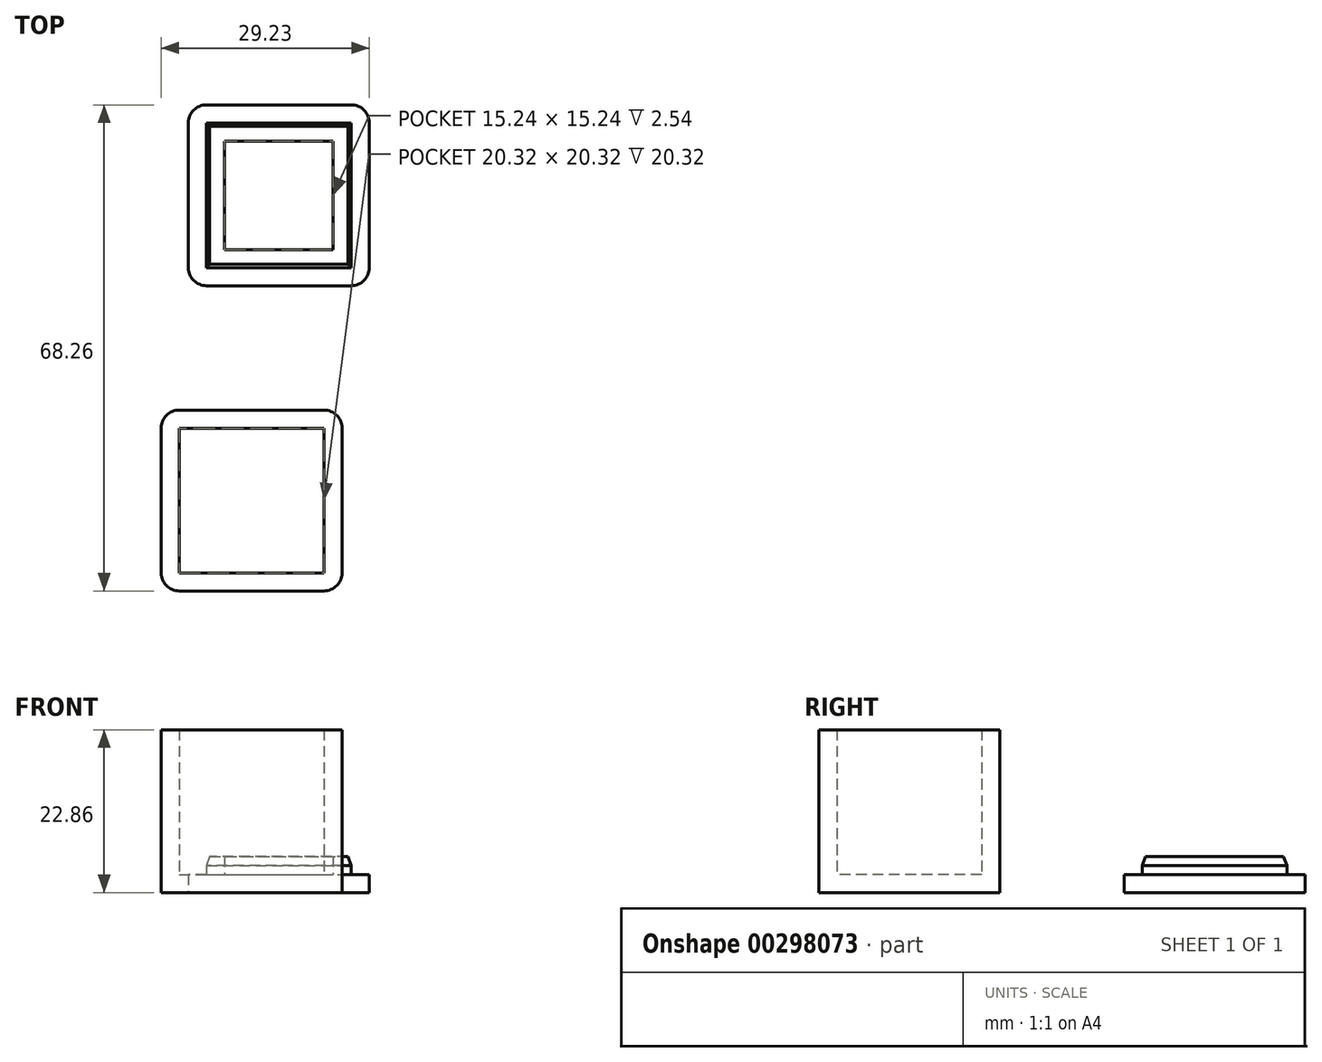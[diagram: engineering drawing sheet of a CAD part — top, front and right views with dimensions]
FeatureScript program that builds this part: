
annotation { "Feature Type Name" : "Feature", "Feature Type Description" : "" }
export const myFeature = defineFeature(function(context is Context, id is Id, definition is map)
    precondition{}
    {
        {
            var Q0;
            Q0=qCreatedBy(makeId("Top.planeOp"),FACE);
            var sketch = newSketch(context, id + "F0", { "sketchPlane" : qUnion([Q0])});
            skLineSegment(sketch, "E0.bottom", {"start": v(-10.16, 12.7) * mm, "end": v(10.16, 12.7) * mm});
            skLineSegment(sketch, "E0.top", {"start": v(-10.16, -12.7) * mm, "end": v(10.16, -12.7) * mm});
            skLineSegment(sketch, "E0.left", {"start": v(-12.7, 10.16) * mm, "end": v(-12.7, -10.16) * mm});
            skLineSegment(sketch, "E0.right", {"start": v(12.7, 10.16) * mm, "end": v(12.7, -10.16) * mm});
            skLineSegment(sketch, "E1.bottom", {"start": v(-10.16, 10.16) * mm, "end": v(10.16, 10.16) * mm});
            skLineSegment(sketch, "E1.top", {"start": v(-10.16, -10.16) * mm, "end": v(10.16, -10.16) * mm});
            skLineSegment(sketch, "E1.left", {"start": v(-10.16, 10.16) * mm, "end": v(-10.16, -10.16) * mm});
            skLineSegment(sketch, "E1.right", {"start": v(10.16, 10.16) * mm, "end": v(10.16, -10.16) * mm});
            skPoint(sketch, "E2.visualSharp", {"position": v(-12.7, 12.7) * mm});
            skArc(sketch, "E2.filletArc", {"start": v(-10.16, 12.7) * mm, "mid": v(-11.96, 11.96) * mm, "end": v(-12.7, 10.16) * mm});
            skPoint(sketch, "E3.visualSharp", {"position": v(12.7, 12.7) * mm});
            skArc(sketch, "E3.filletArc", {"start": v(12.7, 10.16) * mm, "mid": v(11.96, 11.96) * mm, "end": v(10.16, 12.7) * mm});
            skPoint(sketch, "E4.visualSharp", {"position": v(12.7, -12.7) * mm});
            skArc(sketch, "E4.filletArc", {"start": v(10.16, -12.7) * mm, "mid": v(11.96, -11.96) * mm, "end": v(12.7, -10.16) * mm});
            skPoint(sketch, "E5.visualSharp", {"position": v(-12.7, -12.7) * mm});
            skArc(sketch, "E5.filletArc", {"start": v(-12.7, -10.16) * mm, "mid": v(-11.96, -11.96) * mm, "end": v(-10.16, -12.7) * mm});
            skLineSegment(sketch, "E6.bottom", {"start": v(-6.33, 55.56) * mm, "end": v(13.99, 55.56) * mm});
            skLineSegment(sketch, "E6.top", {"start": v(-6.33, 30.16) * mm, "end": v(13.99, 30.16) * mm});
            skLineSegment(sketch, "E6.left", {"start": v(-8.87, 53.02) * mm, "end": v(-8.87, 32.7) * mm});
            skLineSegment(sketch, "E6.right", {"start": v(16.53, 53.02) * mm, "end": v(16.53, 32.7) * mm});
            skLineSegment(sketch, "E7.bottom", {"start": v(-6.33, 53.02) * mm, "end": v(13.99, 53.02) * mm});
            skLineSegment(sketch, "E7.top", {"start": v(-6.33, 32.7) * mm, "end": v(13.99, 32.7) * mm});
            skLineSegment(sketch, "E7.left", {"start": v(-6.33, 53.02) * mm, "end": v(-6.33, 32.7) * mm});
            skLineSegment(sketch, "E7.right", {"start": v(13.99, 53.02) * mm, "end": v(13.99, 32.7) * mm});
            skPoint(sketch, "E8.visualSharp", {"position": v(-8.87, 55.56) * mm});
            skArc(sketch, "E8.filletArc", {"start": v(-6.33, 55.56) * mm, "mid": v(-8.13, 54.82) * mm, "end": v(-8.87, 53.02) * mm});
            skPoint(sketch, "E9.visualSharp", {"position": v(16.53, 55.56) * mm});
            skArc(sketch, "E9.filletArc", {"start": v(16.53, 53.02) * mm, "mid": v(15.78, 54.82) * mm, "end": v(13.99, 55.56) * mm});
            skPoint(sketch, "E10.visualSharp", {"position": v(16.53, 30.16) * mm});
            skArc(sketch, "E10.filletArc", {"start": v(13.99, 30.16) * mm, "mid": v(15.78, 30.9) * mm, "end": v(16.53, 32.7) * mm});
            skPoint(sketch, "E11.visualSharp", {"position": v(-8.87, 30.16) * mm});
            skArc(sketch, "E11.filletArc", {"start": v(-8.87, 32.7) * mm, "mid": v(-8.13, 30.9) * mm, "end": v(-6.33, 30.16) * mm});
            skLineSegment(sketch, "E12.bottom", {"start": v(-3.8, 50.48) * mm, "end": v(11.45, 50.48) * mm});
            skLineSegment(sketch, "E12.top", {"start": v(-3.8, 35.24) * mm, "end": v(11.45, 35.24) * mm});
            skLineSegment(sketch, "E12.left", {"start": v(-3.8, 50.48) * mm, "end": v(-3.8, 35.24) * mm});
            skLineSegment(sketch, "E12.right", {"start": v(11.45, 50.48) * mm, "end": v(11.45, 35.24) * mm});
            skSolve(sketch);
        }
        {
            var Q0;
            Q0=makeQuery(id+"F0.imprint","IMPRINT",FACE,{"disambiguationData":[TD([[makeQuery(id+"F0.imprint","IMPRINT",EDGE,{"derivedFrom":sQuery(id+"F0.wireOp",EDGE,"E0.bottom")}),-1.0]])]});
            extrude(context, id + "F1", {"entities" : qUnion([Q0]), "depth" : 22.86 * mm});
        }
        {
            var Q0;
            Q0=makeQuery(id+"F0.imprint","IMPRINT",FACE,{"disambiguationData":[TD([[makeQuery(id+"F0.imprint","IMPRINT",EDGE,{"derivedFrom":sQuery(id+"F0.wireOp",EDGE,"E1.bottom")}),-1.0]])]});
            extrude(context, id + "F2", {"entities" : qUnion([Q0]), "operationType" : NewBodyOperationType.ADD, "depth" : 2.54 * mm});
        }
        {
            var Q0;
            Q0=makeQuery(id+"F0.imprint","IMPRINT",FACE,{"disambiguationData":[TD([[makeQuery(id+"F0.imprint","IMPRINT",EDGE,{"derivedFrom":sQuery(id+"F0.wireOp",EDGE,"E6.bottom")}),-1.0]])]});
            extrude(context, id + "F3", {"entities" : qUnion([Q0]), "depth" : 2.54 * mm});
        }
        {
            var Q0;
            Q0=makeQuery(id+"F0.imprint","IMPRINT",FACE,{"disambiguationData":[TD([[makeQuery(id+"F0.imprint","IMPRINT",EDGE,{"derivedFrom":sQuery(id+"F0.wireOp",EDGE,"E7.bottom")}),-1.0]])]});
            extrude(context, id + "F4", {"entities" : qUnion([Q0]), "operationType" : NewBodyOperationType.ADD, "depth" : 5.08 * mm});
        }
        {
            var Q0;
            Q0=makeQuery(id+"F0.imprint","IMPRINT",FACE,{"disambiguationData":[TD([[makeQuery(id+"F0.imprint","IMPRINT",EDGE,{"derivedFrom":sQuery(id+"F0.wireOp",EDGE,"E12.bottom")}),-1.0]])]});
            extrude(context, id + "F5", {"entities" : qUnion([Q0]), "operationType" : NewBodyOperationType.ADD, "depth" : 2.54 * mm});
        }
        {
            var Q0;
            Q0=makeQuery(id+"F4.opExtrude","CAP_EDGE",EDGE,{"disambiguationData":[OSD([sQuery(id+"F0.wireOp",EDGE,"E7.right")])],"isStart":false});
            var Q1;
            Q1=makeQuery(id+"F4.opExtrude","CAP_EDGE",EDGE,{"disambiguationData":[OSD([sQuery(id+"F0.wireOp",EDGE,"E7.top")])],"isStart":false});
            var Q2;
            Q2=makeQuery(id+"F4.opExtrude","CAP_EDGE",EDGE,{"disambiguationData":[OSD([sQuery(id+"F0.wireOp",EDGE,"E7.bottom")])],"isStart":false});
            var Q3;
            Q3=makeQuery(id+"F4.opExtrude","CAP_EDGE",EDGE,{"disambiguationData":[OSD([sQuery(id+"F0.wireOp",EDGE,"E7.left")])],"isStart":false});
            chamfer(context, id + "F6", {"entities" : qUnion([Q0, Q1, Q2, Q3]), "chamferType" : ChamferType.OFFSET_ANGLE, "width" : 1.27 * mm, "oppositeDirection" : false, "angle" : 20 * degree, "tangentPropagation" : true});
        }
    });
